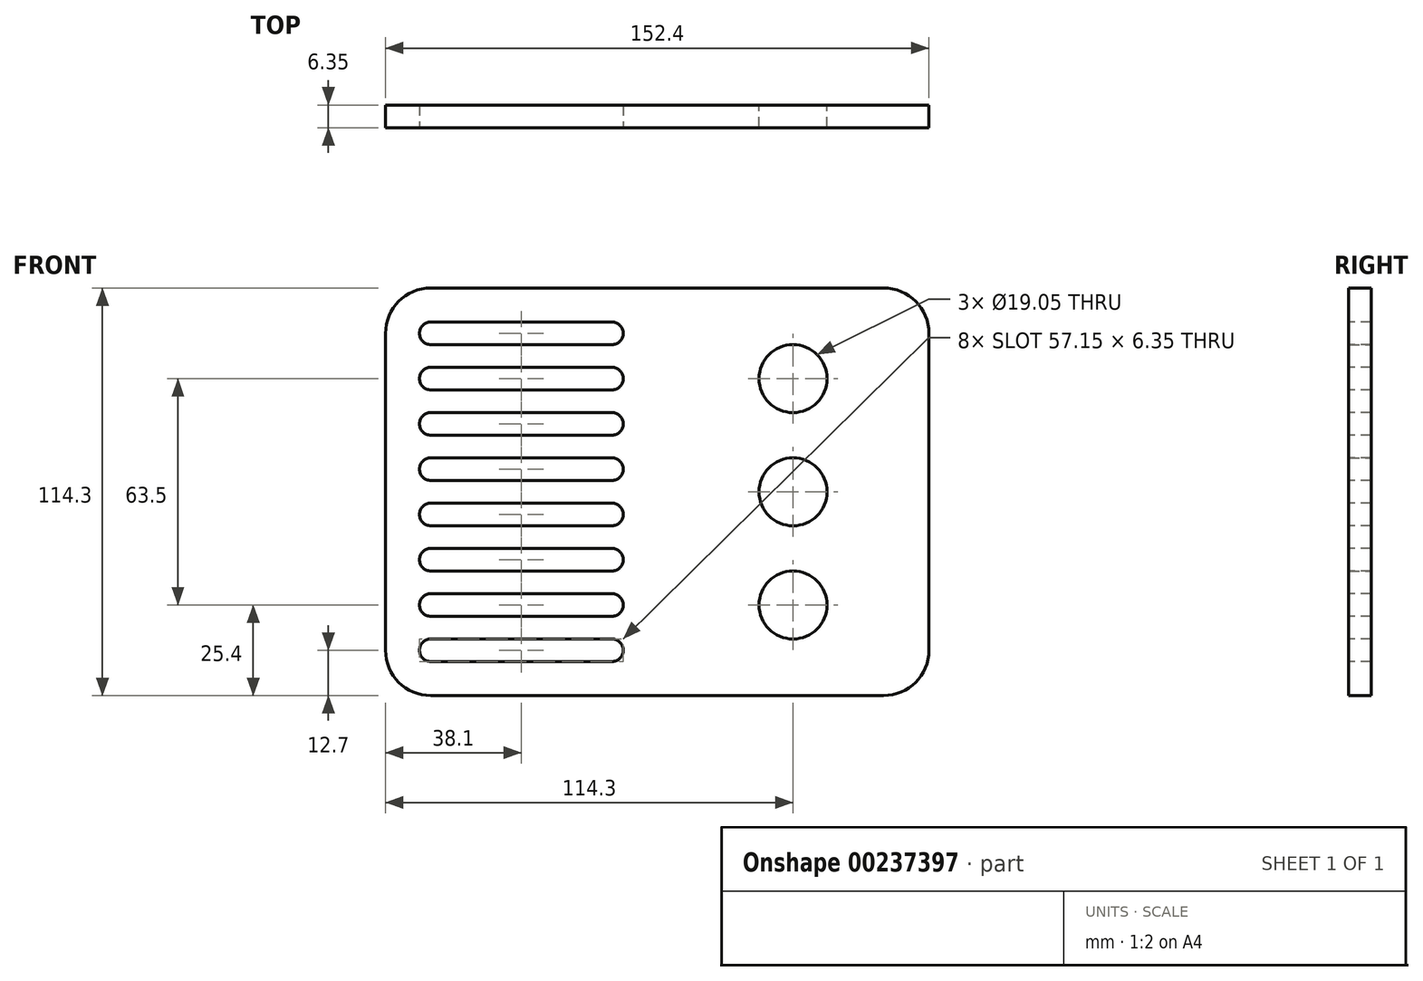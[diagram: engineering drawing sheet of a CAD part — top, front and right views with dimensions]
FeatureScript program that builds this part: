
annotation { "Feature Type Name" : "Feature", "Feature Type Description" : "" }
export const myFeature = defineFeature(function(context is Context, id is Id, definition is map)
    precondition{}
    {
        {
            var Q0;
            Q0=qCreatedBy(makeId("Front.planeOp"),FACE);
            var sketch = newSketch(context, id + "F0", { "sketchPlane" : qUnion([Q0])});
            skLineSegment(sketch, "E0.bottom", {"start": v(76.2, 57.15) * mm, "end": v(-76.2, 57.15) * mm});
            skLineSegment(sketch, "E0.top", {"start": v(76.2, -57.15) * mm, "end": v(-76.2, -57.15) * mm});
            skLineSegment(sketch, "E0.left", {"start": v(76.2, 57.15) * mm, "end": v(76.2, -57.15) * mm});
            skLineSegment(sketch, "E0.right", {"start": v(-76.2, 57.15) * mm, "end": v(-76.2, -57.15) * mm});
            skPoint(sketch, "E0.middle", {"position": v(0, 0) * mm});
            skSolve(sketch);
        }
        {
            var Q0;
            Q0=makeQuery(id+"F0.imprint","IMPRINT",FACE,{"disambiguationData":[TD([[makeQuery(id+"F0.imprint","IMPRINT",EDGE,{"derivedFrom":sQuery(id+"F0.wireOp",EDGE,"E0.bottom")}),1.0]])]});
            extrude(context, id + "F1", {"entities" : qUnion([Q0]), "depth" : 6.35 * mm});
        }
        {
            var Q0;
            Q0=makeQuery(id+"F1.opExtrude","CAP_FACE",FACE,{"disambiguationData":[OSD([sQuery(id+"F0.wireOp",EDGE,"E0.bottom"),sQuery(id+"F0.wireOp",EDGE,"E0.top"),sQuery(id+"F0.wireOp",EDGE,"E0.left"),sQuery(id+"F0.wireOp",EDGE,"E0.right")])],"isStart":false});
            var sketch = newSketch(context, id + "F2", { "sketchPlane" : qUnion([Q0])});
            skLineSegment(sketch, "E1", {"start": v(-63.5, 47.62) * mm, "end": v(-12.7, 47.62) * mm});
            skLineSegment(sketch, "E2", {"start": v(-63.5, 41.27) * mm, "end": v(-12.7, 41.27) * mm});
            skPoint(sketch, "E3", {"position": v(-63.5, 44.45) * mm});
            skPoint(sketch, "E4", {"position": v(-12.7, 44.45) * mm});
            skArc(sketch, "E5", {"start": v(-63.5, 47.62) * mm, "mid": v(-66.68, 44.45) * mm, "end": v(-63.5, 41.27) * mm});
            skArc(sketch, "E6", {"start": v(-12.7, 41.27) * mm, "mid": v(-9.52, 44.45) * mm, "end": v(-12.7, 47.62) * mm});
            skLineSegment(sketch, "E7.MirrorCS", {"start": v(-63.5, -41.27) * mm, "end": v(-12.7, -41.27) * mm});
            skLineSegment(sketch, "E8.MirrorCS", {"start": v(-63.5, -47.62) * mm, "end": v(-12.7, -47.62) * mm});
            skArc(sketch, "E9.MirrorCS", {"start": v(-12.7, -41.27) * mm, "mid": v(-9.52, -44.45) * mm, "end": v(-12.7, -47.62) * mm});
            skArc(sketch, "E10.MirrorCS", {"start": v(-63.5, -47.62) * mm, "mid": v(-66.68, -44.45) * mm, "end": v(-63.5, -41.27) * mm});
            skLineSegment(sketch, "E11.MirrorCS", {"start": v(-63.5, 28.57) * mm, "end": v(-12.7, 28.57) * mm});
            skLineSegment(sketch, "E12.MirrorCS", {"start": v(-63.5, 34.92) * mm, "end": v(-12.7, 34.92) * mm});
            skArc(sketch, "E13.MirrorCS", {"start": v(-63.5, 28.58) * mm, "mid": v(-66.68, 31.75) * mm, "end": v(-63.5, 34.93) * mm});
            skArc(sketch, "E14.MirrorCS", {"start": v(-12.7, 34.92) * mm, "mid": v(-9.53, 31.75) * mm, "end": v(-12.7, 28.57) * mm});
            skLineSegment(sketch, "E15.MirrorCS", {"start": v(-63.5, -28.57) * mm, "end": v(-12.7, -28.57) * mm});
            skLineSegment(sketch, "E16.MirrorCS", {"start": v(-63.5, -34.92) * mm, "end": v(-12.7, -34.92) * mm});
            skArc(sketch, "E17.MirrorCS", {"start": v(-12.7, -34.92) * mm, "mid": v(-9.53, -31.75) * mm, "end": v(-12.7, -28.57) * mm});
            skArc(sketch, "E18.MirrorCS", {"start": v(-63.5, -28.58) * mm, "mid": v(-66.68, -31.75) * mm, "end": v(-63.5, -34.93) * mm});
            skLineSegment(sketch, "E19.MirrorCS", {"start": v(-63.5, 22.22) * mm, "end": v(-12.7, 22.22) * mm});
            skArc(sketch, "E20.MirrorCS", {"start": v(-63.5, 22.22) * mm, "mid": v(-66.67, 19.05) * mm, "end": v(-63.5, 15.87) * mm});
            skLineSegment(sketch, "E21.MirrorCS", {"start": v(-63.5, 15.87) * mm, "end": v(-12.7, 15.87) * mm});
            skArc(sketch, "E22.MirrorCS", {"start": v(-12.7, 15.87) * mm, "mid": v(-9.53, 19.05) * mm, "end": v(-12.7, 22.22) * mm});
            skLineSegment(sketch, "E23.MirrorCS", {"start": v(-63.5, -15.87) * mm, "end": v(-12.7, -15.87) * mm});
            skArc(sketch, "E24.MirrorCS", {"start": v(-63.5, -22.22) * mm, "mid": v(-66.67, -19.05) * mm, "end": v(-63.5, -15.87) * mm});
            skLineSegment(sketch, "E25.MirrorCS", {"start": v(-63.5, -22.22) * mm, "end": v(-12.7, -22.22) * mm});
            skArc(sketch, "E26.MirrorCS", {"start": v(-12.7, -15.87) * mm, "mid": v(-9.53, -19.05) * mm, "end": v(-12.7, -22.22) * mm});
            skLineSegment(sketch, "E27.MirrorCS", {"start": v(-63.5, 9.52) * mm, "end": v(-12.7, 9.52) * mm});
            skArc(sketch, "E28.MirrorCS", {"start": v(-63.5, 3.17) * mm, "mid": v(-66.67, 6.35) * mm, "end": v(-63.5, 9.53) * mm});
            skLineSegment(sketch, "E29.MirrorCS", {"start": v(-63.5, 3.17) * mm, "end": v(-12.7, 3.17) * mm});
            skArc(sketch, "E30.MirrorCS", {"start": v(-12.7, 9.52) * mm, "mid": v(-9.53, 6.35) * mm, "end": v(-12.7, 3.17) * mm});
            skLineSegment(sketch, "E31.MirrorCS", {"start": v(-63.5, -9.52) * mm, "end": v(-12.7, -9.52) * mm});
            skArc(sketch, "E32.MirrorCS", {"start": v(-63.5, -3.17) * mm, "mid": v(-66.67, -6.35) * mm, "end": v(-63.5, -9.53) * mm});
            skArc(sketch, "E33.MirrorCS", {"start": v(-12.7, -9.52) * mm, "mid": v(-9.53, -6.35) * mm, "end": v(-12.7, -3.17) * mm});
            skLineSegment(sketch, "E34.MirrorCS", {"start": v(-63.5, -3.17) * mm, "end": v(-12.7, -3.17) * mm});
            skSolve(sketch);
        }
        {
            var Q0;
            Q0 = qSketchRegion(id + "F2", true);
            extrude(context, id + "F3", {"entities" : qUnion([Q0]), "operationType" : NewBodyOperationType.REMOVE, "endBound" : BoundingType.THROUGH_ALL, "oppositeDirection" : true, "depth" : 25.4 * mm});
        }
        {
            var Q0;
            Q0=qCreatedBy(makeId("Front.planeOp"),FACE);
            var sketch = newSketch(context, id + "F4", { "sketchPlane" : qUnion([Q0])});
            skPoint(sketch, "E35", {"position": v(38.1, 31.75) * mm});
            skPoint(sketch, "E36", {"position": v(38.1, 0) * mm});
            skPoint(sketch, "E37", {"position": v(38.1, -31.75) * mm});
            skSolve(sketch);
        }
        {
            var Q0;
            Q0=sQuery(id+"F4.wireOp",VERTEX,"E35");
            var Q1;
            Q1=sQuery(id+"F4.wireOp",VERTEX,"E36");
            var Q2;
            Q2=sQuery(id+"F4.wireOp",VERTEX,"E37");
            var Q3;
            Q3=makeQuery(id+"F1.opExtrude","SWEPT_BODY",BODY,{"disambiguationData":[OSD([sQuery(id+"F0.wireOp",EDGE,"E0.bottom"),sQuery(id+"F0.wireOp",EDGE,"E0.top"),sQuery(id+"F0.wireOp",EDGE,"E0.left"),sQuery(id+"F0.wireOp",EDGE,"E0.right")])]});
            hole(context, id + "F5", {"style" : HoleStyle.SIMPLE, "endStyle" : HoleEndStyle.THROUGH, "oppositeDirection" : true, "holeDiameter" : 19.05 * mm, "locations" : qUnion([Q0, Q1, Q2]), "scope" : qUnion([Q3]), "isTappedThrough" : true});
        }
        {
            var Q0;
            Q0=makeQuery(id+"F1.opExtrude","SWEPT_EDGE",EDGE,{"disambiguationData":[OSD([sQuery(id+"F0.wireOp",EDGE,"E0.bottom"),sQuery(id+"F0.wireOp",EDGE,"E0.left")])]});
            var Q1;
            Q1=makeQuery(id+"F1.opExtrude","SWEPT_EDGE",EDGE,{"disambiguationData":[OSD([sQuery(id+"F0.wireOp",EDGE,"E0.top"),sQuery(id+"F0.wireOp",EDGE,"E0.left")])]});
            fillet(context, id + "F6", {"entities" : qUnion([Q0, Q1]), "radius" : 12.7 * mm, "tangentPropagation" : true, "allowEdgeOverflow" : false});
        }
        {
            var Q0;
            Q0=makeQuery(id+"F1.opExtrude","SWEPT_EDGE",EDGE,{"disambiguationData":[OSD([sQuery(id+"F0.wireOp",EDGE,"E0.bottom"),sQuery(id+"F0.wireOp",EDGE,"E0.right")])]});
            var Q1;
            Q1=makeQuery(id+"F1.opExtrude","SWEPT_EDGE",EDGE,{"disambiguationData":[OSD([sQuery(id+"F0.wireOp",EDGE,"E0.top"),sQuery(id+"F0.wireOp",EDGE,"E0.right")])]});
            fillet(context, id + "F7", {"entities" : qUnion([Q0, Q1]), "radius" : 12.7 * mm, "tangentPropagation" : true, "allowEdgeOverflow" : false});
        }
    });
